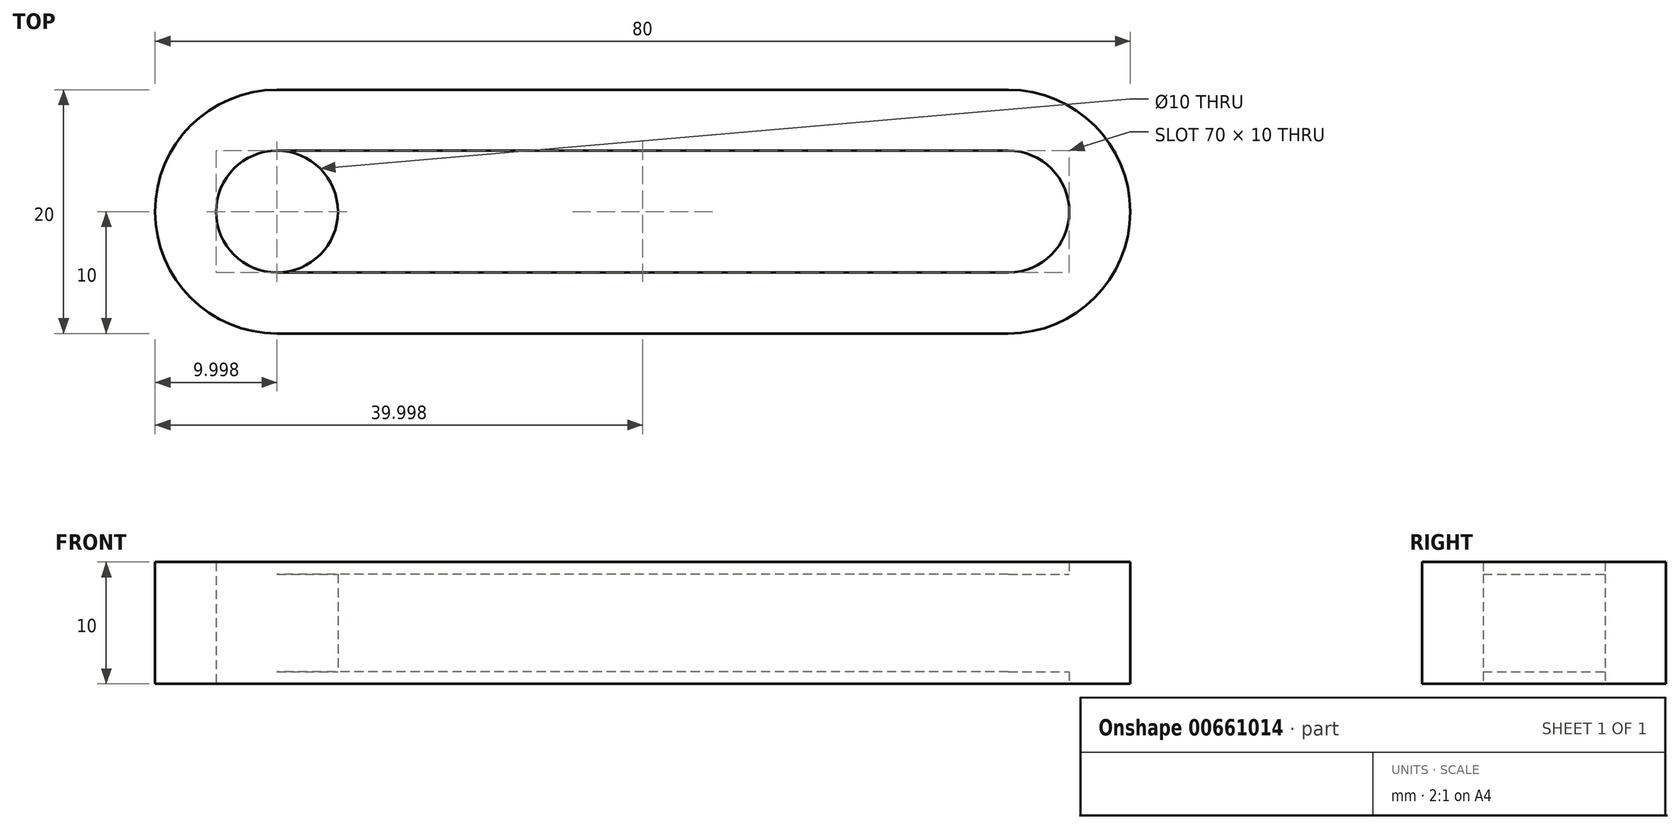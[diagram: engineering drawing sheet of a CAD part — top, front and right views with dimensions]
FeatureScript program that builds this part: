
annotation { "Feature Type Name" : "Feature", "Feature Type Description" : "" }
export const myFeature = defineFeature(function(context is Context, id is Id, definition is map)
    precondition{}
    {
        {
            var Q0;
            Q0=qCreatedBy(makeId("Top.planeOp"),FACE);
            var sketch = newSketch(context, id + "F0", { "sketchPlane" : qUnion([Q0])});
            skArc(sketch, "E0", {"start": v(36.02, -5) * mm, "mid": v(41.02, 0) * mm, "end": v(36.02, 5) * mm});
            skLineSegment(sketch, "E1", {"start": v(36.02, 0) * mm, "end": v(36.02, 5) * mm});
            skLineSegment(sketch, "E2", {"start": v(36.02, 5) * mm, "end": v(-23.98, 5) * mm});
            skLineSegment(sketch, "E3.0", {"start": v(36.02, -5) * mm, "end": v(-23.98, -5) * mm});
            skArc(sketch, "E4", {"start": v(-23.98, 5) * mm, "mid": v(-28.98, 0) * mm, "end": v(-23.98, -5) * mm});
            skLineSegment(sketch, "E5.0", {"start": v(36.02, 10) * mm, "end": v(-23.98, 10) * mm});
            skLineSegment(sketch, "E6.MirrorCS", {"start": v(36.02, -10) * mm, "end": v(-23.98, -10) * mm});
            skArc(sketch, "E7", {"start": v(36.02, 10) * mm, "mid": v(46.02, 0) * mm, "end": v(36.02, -10) * mm});
            skArc(sketch, "E8", {"start": v(-23.98, 10) * mm, "mid": v(-33.98, 0) * mm, "end": v(-23.98, -10) * mm});
            skArc(sketch, "E9", {"start": v(-23.98, -5) * mm, "mid": v(-18.98, 0) * mm, "end": v(-23.98, 5) * mm});
            skSolve(sketch);
        }
        {
            var Q0;
            Q0=makeQuery(id+"F0.imprint","IMPRINT",FACE,{"disambiguationData":[TD([[makeQuery(id+"F0.imprint","IMPRINT",EDGE,{"derivedFrom":sQuery(id+"F0.wireOp",EDGE,"E0")}),1.0]])]});
            extrude(context, id + "F1", {"entities" : qUnion([Q0]), "endBound" : BoundingType.SYMMETRIC, "depth" : 8 * mm, "offsetDistance" : 25 * mm});
        }
        {
            var Q0;
            Q0 = qSketchRegion(id + "F0", true);
            extrude(context, id + "F2", {"entities" : qUnion([Q0]), "operationType" : NewBodyOperationType.ADD, "endBound" : BoundingType.SYMMETRIC, "depth" : 10 * mm, "offsetDistance" : 25 * mm});
        }
    });
